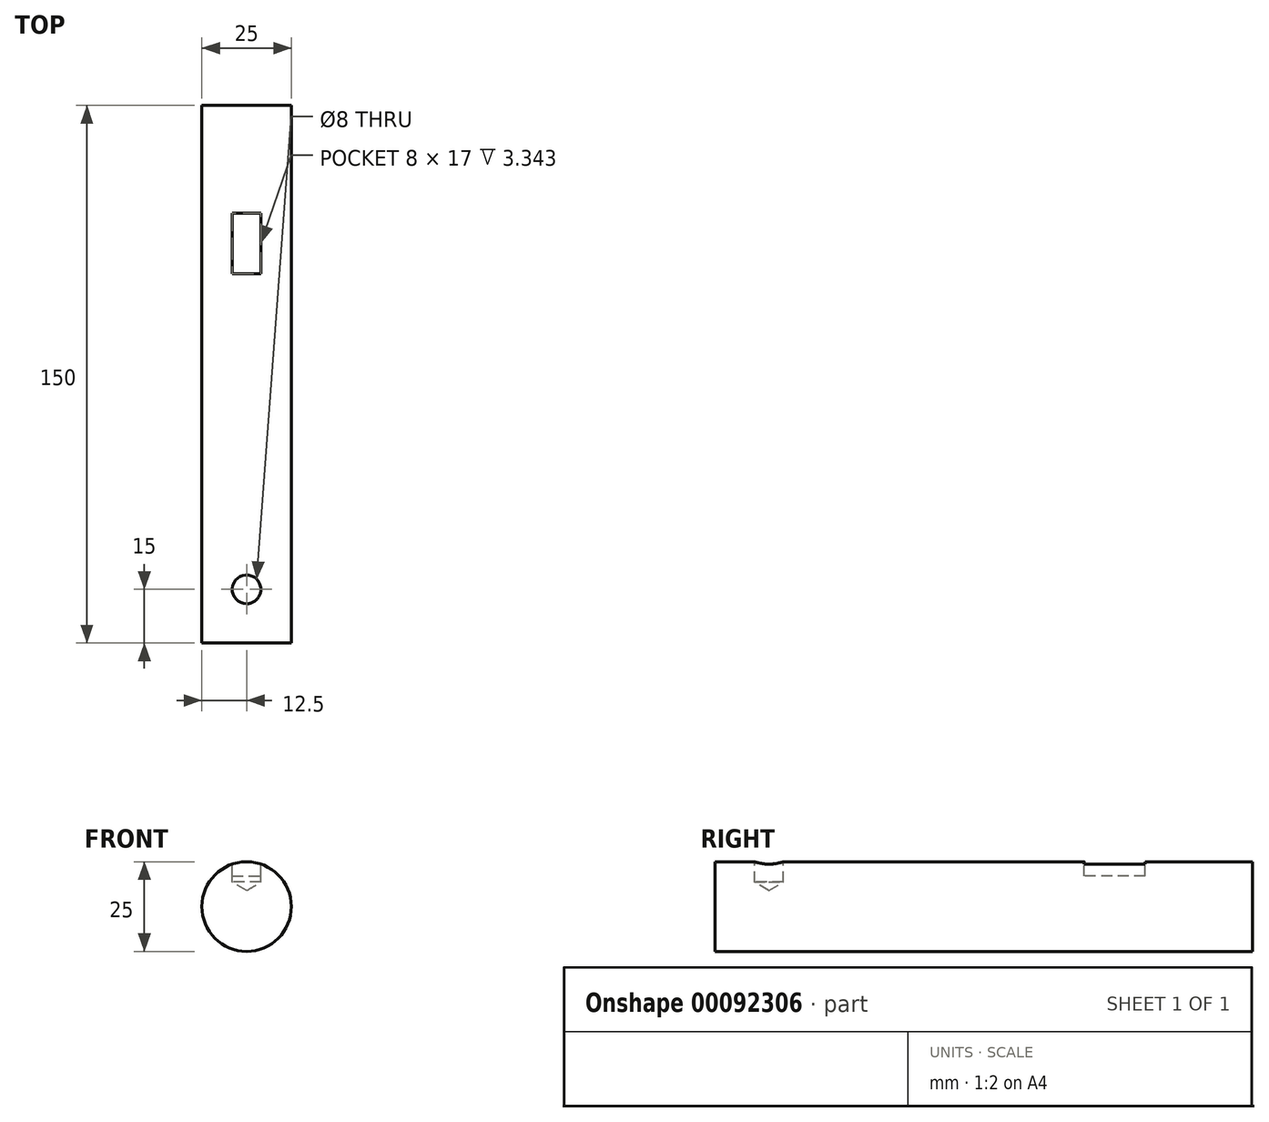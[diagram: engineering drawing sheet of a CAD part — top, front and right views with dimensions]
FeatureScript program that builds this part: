
annotation { "Feature Type Name" : "Feature", "Feature Type Description" : "" }
export const myFeature = defineFeature(function(context is Context, id is Id, definition is map)
    precondition{}
    {
        {
            var Q0;
            Q0=qCreatedBy(makeId("Front.planeOp"),FACE);
            var sketch = newSketch(context, id + "F0", { "sketchPlane" : qUnion([Q0])});
            skCircle(sketch, "E0", {"center": v(0, 0) * mm, "radius": 12.5 * mm});
            skSolve(sketch);
        }
        {
            var Q0;
            Q0=makeQuery(id+"F0.imprint","IMPRINT",FACE,{"disambiguationData":[TD([[makeQuery(id+"F0.imprint","IMPRINT",EDGE,{"derivedFrom":sQuery(id+"F0.wireOp",EDGE,"E0")}),1.0]])]});
            extrude(context, id + "F1", {"entities" : qUnion([Q0]), "depth" : 150 * mm});
        }
        {
            var Q0;
            Q0=qCreatedBy(makeId("Top.planeOp"),FACE);
            cPlane(context, id + "F2", {"entities" : qUnion([Q0]), "cplaneType" : CPlaneType.OFFSET, "offset" : 12.5 * mm, "width" : 150 * mm, "height" : 150 * mm});
        }
        {
            var Q0;
            Q0=qCreatedBy(id+"F2.planeOp",FACE);
            var sketch = newSketch(context, id + "F3", { "sketchPlane" : qUnion([Q0])});
            skLineSegment(sketch, "E1.bottom", {"start": v(0, -30) * mm, "end": v(4, -30) * mm});
            skLineSegment(sketch, "E1.top", {"start": v(0, -47) * mm, "end": v(4, -47) * mm});
            skLineSegment(sketch, "E1.right", {"start": v(4, -30) * mm, "end": v(4, -47) * mm});
            skLineSegment(sketch, "E2.MirrorCS", {"start": v(-4, -30) * mm, "end": v(-4, -47) * mm});
            skLineSegment(sketch, "E3.MirrorCS", {"start": v(0, -30) * mm, "end": v(-4, -30) * mm});
            skLineSegment(sketch, "E4.MirrorCS", {"start": v(0, -47) * mm, "end": v(-4, -47) * mm});
            skSolve(sketch);
        }
        {
            var Q0;
            Q0=makeQuery(id+"F3.imprint","IMPRINT",FACE,{"disambiguationData":[TD([[makeQuery(id+"F3.imprint","IMPRINT",EDGE,{"derivedFrom":sQuery(id+"F3.wireOp",EDGE,"E1.bottom")}),-1.0]])]});
            extrude(context, id + "F4", {"entities" : qUnion([Q0]), "operationType" : NewBodyOperationType.REMOVE, "oppositeDirection" : true, "depth" : 4 * mm});
        }
        {
            var Q0;
            Q0=qCreatedBy(id+"F2.planeOp",FACE);
            var sketch = newSketch(context, id + "F5", { "sketchPlane" : qUnion([Q0])});
            skLineSegment(sketch, "E5", {"start": v(0, -150) * mm, "end": v(0, -135) * mm});
            skSolve(sketch);
        }
        {
            var Q0;
            Q0=sQuery(id+"F5.wireOp",VERTEX,"E5.end");
            var Q1;
            Q1=makeQuery(id+"F1.opExtrude","SWEPT_BODY",BODY,{"disambiguationData":[OSD([sQuery(id+"F0.wireOp",EDGE,"E0")])]});
            hole(context, id + "F6", {"style" : HoleStyle.SIMPLE, "endStyle" : HoleEndStyle.BLIND, "holeDiameter" : 8 * mm, "holeDepth" : 5 * mm, "locations" : qUnion([Q0]), "scope" : qUnion([Q1])});
        }
    });
